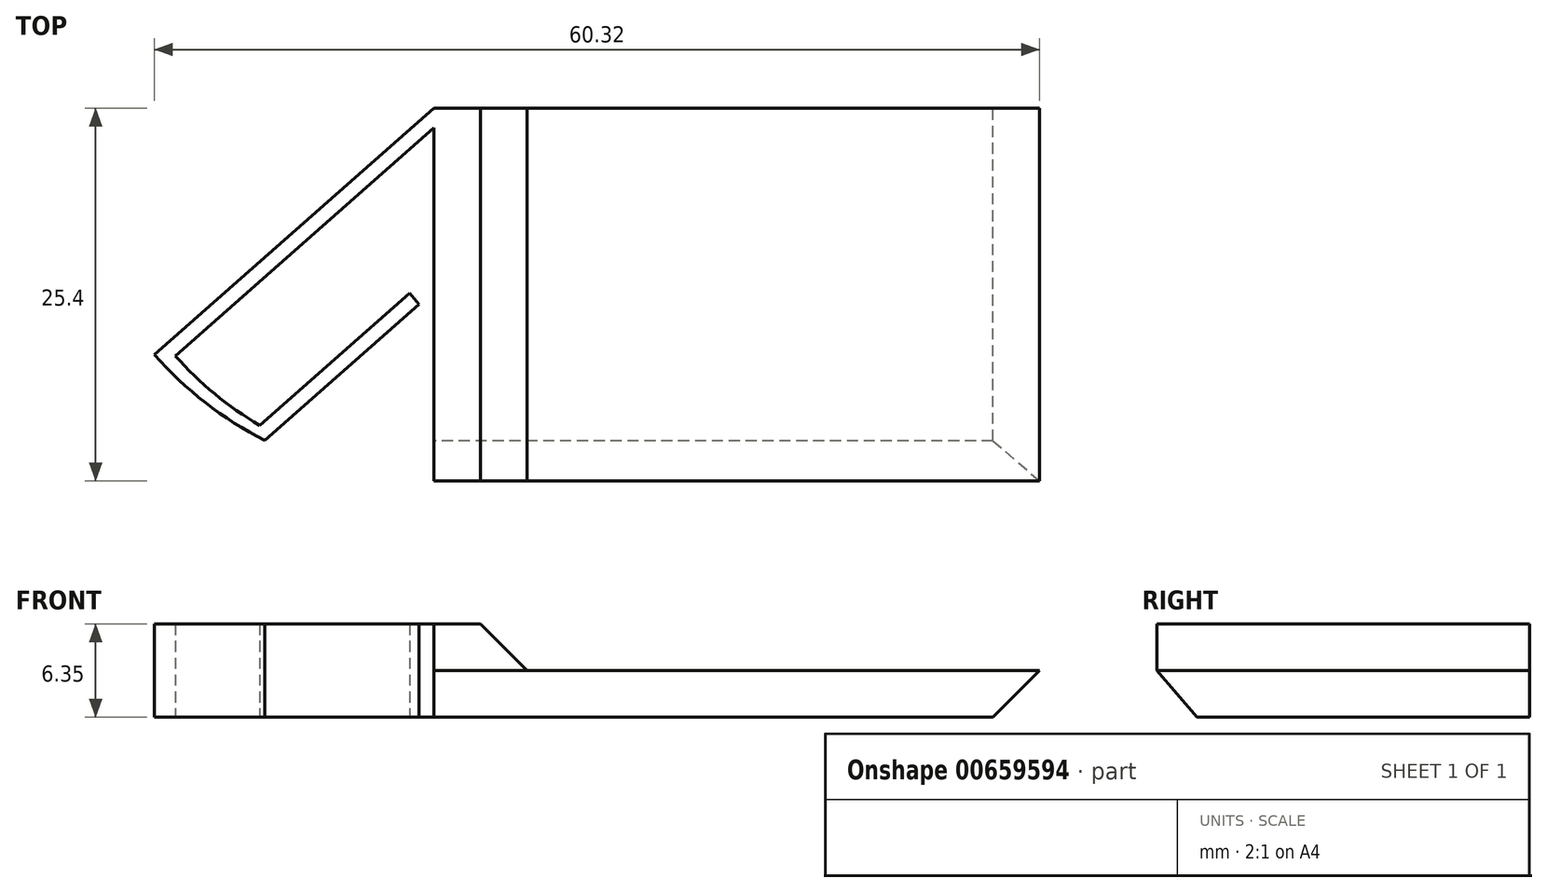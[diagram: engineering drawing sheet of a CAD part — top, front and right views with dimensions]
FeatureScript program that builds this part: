
annotation { "Feature Type Name" : "Feature", "Feature Type Description" : "" }
export const myFeature = defineFeature(function(context is Context, id is Id, definition is map)
    precondition{}
    {
        {
            var Q0;
            Q0=qCreatedBy(makeId("Top.planeOp"),FACE);
            var sketch = newSketch(context, id + "F0", { "sketchPlane" : qUnion([Q0])});
            skLineSegment(sketch, "E0.bottom", {"start": v(28.58, -12.7) * mm, "end": v(-28.58, -12.7) * mm});
            skLineSegment(sketch, "E0.top", {"start": v(28.58, 12.7) * mm, "end": v(-28.58, 12.7) * mm});
            skLineSegment(sketch, "E0.left", {"start": v(28.58, -12.7) * mm, "end": v(28.58, 12.7) * mm});
            skLineSegment(sketch, "E0.right", {"start": v(-28.57, -12.7) * mm, "end": v(-28.57, 12.7) * mm});
            skPoint(sketch, "E0.middle", {"position": v(0, 0) * mm});
            skLineSegment(sketch, "E1", {"start": v(-9.53, 11.37) * mm, "end": v(-9.52, -12.7) * mm});
            skLineSegment(sketch, "E2", {"start": v(0, -12.7) * mm, "end": v(0, 12.7) * mm});
            skPoint(sketch, "E3", {"position": v(-22.22, -12.7) * mm});
            skLineSegment(sketch, "E4", {"start": v(-9.53, 12.7) * mm, "end": v(-28.57, -4.1) * mm});
            skPoint(sketch, "E5", {"position": v(-19.05, -12.7) * mm});
            skArc(sketch, "E6", {"start": v(-28.57, -4.1) * mm, "mid": v(-25.09, -7.37) * mm, "end": v(-21.05, -9.94) * mm});
            skLineSegment(sketch, "E7", {"start": v(-21.05, -9.94) * mm, "end": v(-10.53, -0.66) * mm});
            skLineSegment(sketch, "E8", {"start": v(-10.53, -0.66) * mm, "end": v(-11.19, 0.1) * mm});
            skLineSegment(sketch, "E9", {"start": v(-11.19, 0.1) * mm, "end": v(-11.19, 0.1) * mm});
            skLineSegment(sketch, "E10", {"start": v(-9.53, 11.37) * mm, "end": v(-27.15, -4.18) * mm});
            skArc(sketch, "E11", {"start": v(-27.15, -4.18) * mm, "mid": v(-24.46, -6.77) * mm, "end": v(-21.4, -8.91) * mm});
            skLineSegment(sketch, "E12", {"start": v(-21.4, -8.91) * mm, "end": v(-11.19, 0.1) * mm});
            skSolve(sketch);
        }
        {
            var Q0;
            {var subQ0=sQuery(id+"F0.wireOp",EDGE,"E0.left");Q0=makeQuery(id+"F0.imprint","IMPRINT",FACE,{"disambiguationData":[TD([[makeQuery(id+"F0.imprint","IMPRINT",EDGE,{"derivedFrom":subQ0}),1.0]])]});}
            var Q1;
            {var subQ1=sQuery(id+"F0.wireOp",EDGE,"E1");Q1=makeQuery(id+"F0.imprint","IMPRINT",FACE,{"disambiguationData":[TD([[makeQuery(id+"F0.imprint","IMPRINT",EDGE,{"derivedFrom":subQ1}),1.0]])]});}
            var Q2;
            {var subQ0=sQuery(id+"F0.wireOp",EDGE,"Ll8NUgnO-918t-zldm-zNWz-RsUZQomu35K8");Q2=makeQuery(id+"F0.imprint","IMPRINT",FACE,{"disambiguationData":[TD([[makeQuery(id+"F0.imprint","IMPRINT",EDGE,{"derivedFrom":subQ0}),1.0]])]});}
            extrude(context, id + "F1", {"entities" : qUnion([Q0, Q1, Q2]), "depth" : 3.17 * mm, "offsetDistance" : 25.4 * mm});
        }
        {
            var Q0;
            {var subQ1=sQuery(id+"F0.wireOp",EDGE,"E1");Q0=makeQuery(id+"F0.imprint","IMPRINT",FACE,{"disambiguationData":[TD([[makeQuery(id+"F0.imprint","IMPRINT",EDGE,{"derivedFrom":subQ1}),1.0]])]});}
            extrude(context, id + "F2", {"entities" : qUnion([Q0]), "operationType" : NewBodyOperationType.ADD, "depth" : 6.35 * mm, "offsetDistance" : 25.4 * mm});
        }
        {
            var Q0;
            Q0=makeQuery(id+"F2.opExtrude","CAP_EDGE",EDGE,{"disambiguationData":[OSD([sQuery(id+"F0.wireOp",EDGE,"E2")])],"isStart":false});
            chamfer(context, id + "F3", {"entities" : qUnion([Q0]), "width" : 6.35 * mm, "tangentPropagation" : true});
        }
        {
            var Q0;
            {var subQ0=sQuery(id+"F0.wireOp",EDGE,"E1");Q0=makeQuery(id+"F2.boolean.opBoolean","MERGE",FACE,{"derivedFrom":[makeQuery(id+"F1.opExtrude","SWEPT_FACE",FACE,{"disambiguationData":[OSD([subQ0])]}),makeQuery(id+"F2.opExtrude","SWEPT_FACE",FACE,{"disambiguationData":[OSD([subQ0])]})]});}
            var sketch = newSketch(context, id + "F4", { "sketchPlane" : qUnion([Q0])});
            skLineSegment(sketch, "E13", {"start": v(12.7, 0) * mm, "end": v(12.7, 3.18) * mm});
            skLineSegment(sketch, "E14", {"start": v(12.7, 3.18) * mm, "end": v(9.96, 0) * mm});
            skLineSegment(sketch, "E15", {"start": v(9.96, 0) * mm, "end": v(12.7, 0) * mm});
            skSolve(sketch);
        }
        {
            var Q0;
            {var subQ0=sQuery(id+"F0.wireOp",EDGE,"E0.top");Q0=makeQuery(id+"F2.boolean.opBoolean","MERGE",FACE,{"derivedFrom":[makeQuery(id+"F1.opExtrude","SWEPT_FACE",FACE,{"disambiguationData":[OSD([subQ0])]}),makeQuery(id+"F2.opExtrude","SWEPT_FACE",FACE,{"disambiguationData":[OSD([subQ0])]})]});}
            var sketch = newSketch(context, id + "F5", { "sketchPlane" : qUnion([Q0])});
            skLineSegment(sketch, "E16", {"start": v(-28.58, 3.18) * mm, "end": v(-31.75, 3.18) * mm});
            skLineSegment(sketch, "E17", {"start": v(-31.75, 3.18) * mm, "end": v(-28.58, 0) * mm});
            skLineSegment(sketch, "E18", {"start": v(-28.58, 0) * mm, "end": v(-28.58, 3.18) * mm});
            skSolve(sketch);
        }
        {
            var Q0;
            Q0=makeQuery(id+"F5.imprint","IMPRINT",FACE,{"disambiguationData":[TD([[makeQuery(id+"F5.imprint","IMPRINT",EDGE,{"derivedFrom":sQuery(id+"F5.wireOp",EDGE,"E18")}),1.0]])]});
            var Q1;
            Q1=makeQuery(id+"F5.imprint","IMPRINT",FACE,{"disambiguationData":[TD([[makeQuery(id+"F5.imprint","IMPRINT",EDGE,{"derivedFrom":sQuery(id+"F5.wireOp",EDGE,"E16")}),1.0]])]});
            extrude(context, id + "F6", {"entities" : qUnion([Q0, Q1]), "operationType" : NewBodyOperationType.ADD, "oppositeDirection" : true, "depth" : 25.4 * mm, "offsetDistance" : 25.4 * mm});
        }
        {
            var Q0;
            Q0=makeQuery(id+"F4.imprint","IMPRINT",FACE,{"disambiguationData":[TD([[makeQuery(id+"F4.imprint","IMPRINT",EDGE,{"derivedFrom":sQuery(id+"F4.wireOp",EDGE,"E13")}),-1.0]])]});
            extrude(context, id + "F7", {"entities" : qUnion([Q0]), "operationType" : NewBodyOperationType.REMOVE, "oppositeDirection" : true, "depth" : 50.8 * mm, "offsetDistance" : 25.4 * mm});
        }
    });
